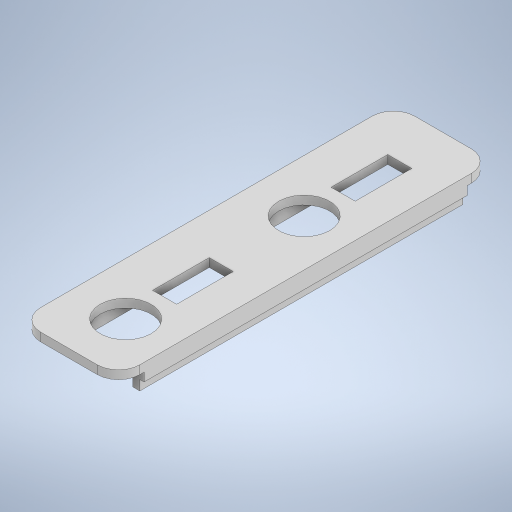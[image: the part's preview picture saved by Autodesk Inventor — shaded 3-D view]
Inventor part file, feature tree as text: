
AUTODESK INVENTOR PART (.ipt)
format: ipt  version: 2024.1 (Build 281209000, 209)  size: 323,584 bytes
history: native  units: mm
features: extrude x3, sketch x2, other x1
ambient origin geometry x8: Origin, YZ Plane, XZ Plane, XY Plane, X Axis, Y Axis, Z Axis, Center Point
bodies: Body1 (feature_tree)
feature tree (6):
  other  "Sólido1"
  extrude  "Extrusión1"  Depth=132.0mm
  sketch  "Boceto2"  dims[d2=7.5mm d5=8.5mm d8=20.0mm d9=12.0mm d10=43.0mm d11=16.5mm d12=13.5mm d13=16.5mm d15=18.0mm d16=13.5mm d17=3.0mm d18=0.0mm d19=4.0mm d20=114.0mm d21=2.5mm d22=2.5mm d23=24.0mm d24=6.5mm d25=0.0mm d26=3.0mm d27=0.0mm d28=0.5mm d29=0.872665mm]
  extrude  "Extrusión2"  Depth=8.5mm
  extrude  "Extrusión3"  Depth=20.0mm
  sketch  "Boceto1"  dims[d0=35.0mm d1=132.0mm]
